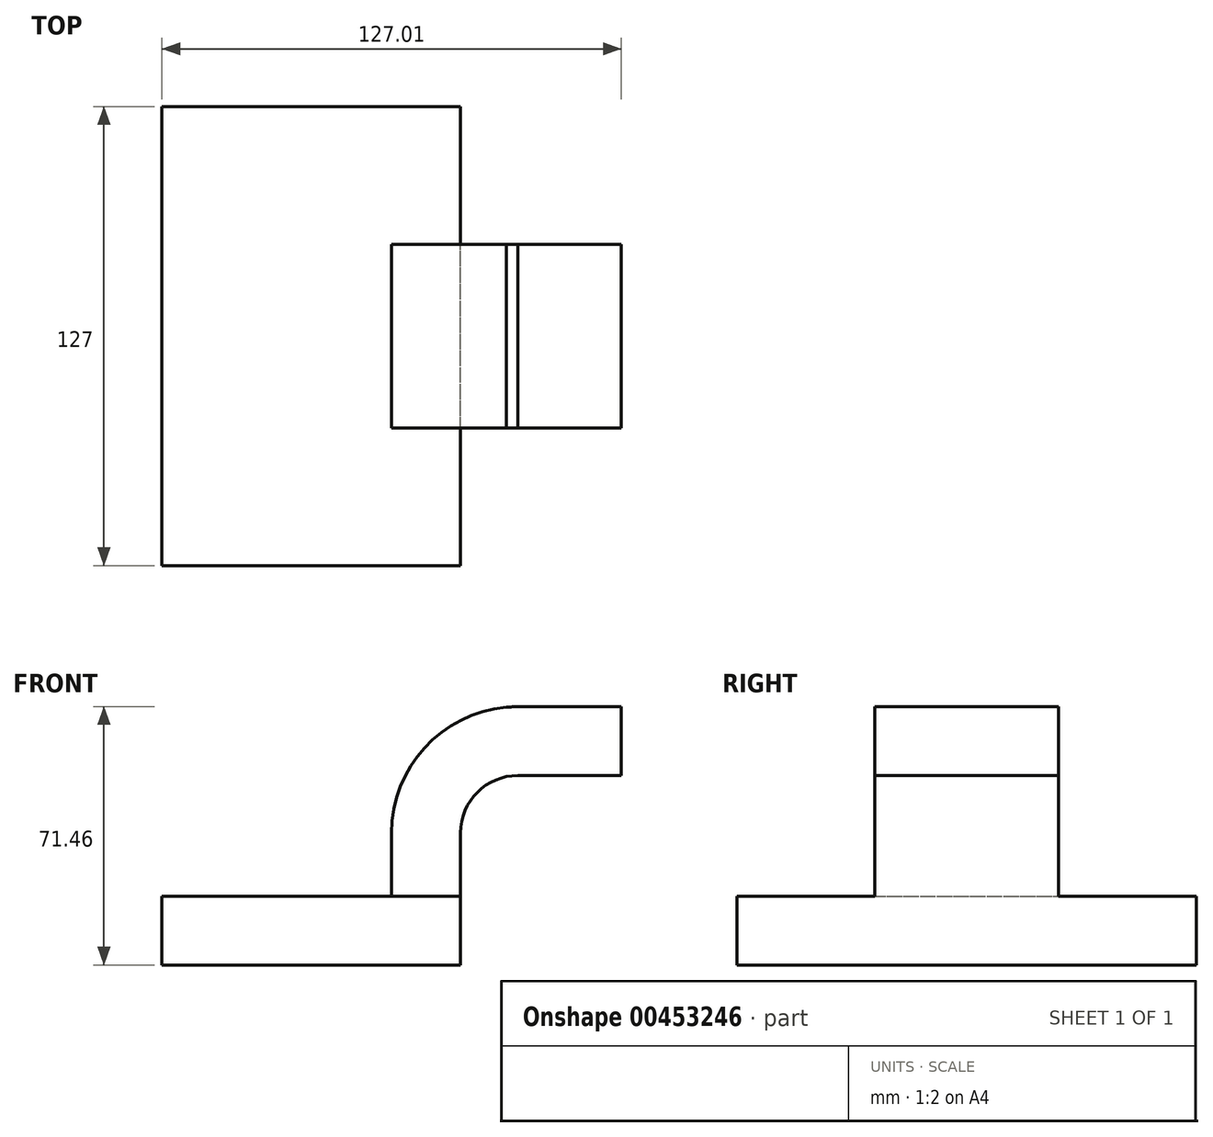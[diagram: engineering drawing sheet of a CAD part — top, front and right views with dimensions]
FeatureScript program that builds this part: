
annotation { "Feature Type Name" : "Feature", "Feature Type Description" : "" }
export const myFeature = defineFeature(function(context is Context, id is Id, definition is map)
    precondition{}
    {
        {
            var Q0;
            Q0=qCreatedBy(makeId("Front.planeOp"),FACE);
            var sketch = newSketch(context, id + "F0", { "sketchPlane" : qUnion([Q0])});
            skLineSegment(sketch, "E0.rect.bottom", {"start": v(-41.28, 9.52) * mm, "end": v(41.28, 9.52) * mm});
            skLineSegment(sketch, "E0.rect.top", {"start": v(-41.28, -9.52) * mm, "end": v(41.28, -9.52) * mm});
            skLineSegment(sketch, "E0.rect.left", {"start": v(-41.28, 9.52) * mm, "end": v(-41.28, -9.52) * mm});
            skLineSegment(sketch, "E0.rect.right", {"start": v(41.28, 9.52) * mm, "end": v(41.28, -9.52) * mm});
            skPoint(sketch, "E0.rect.middle", {"position": v(0, 0) * mm});
            skLineSegment(sketch, "E1", {"start": v(41.28, 9.52) * mm, "end": v(41.28, 27) * mm});
            skArc(sketch, "E2", {"start": v(41.28, 27) * mm, "mid": v(45.92, 38.23) * mm, "end": v(57.15, 42.88) * mm});
            skLineSegment(sketch, "E3", {"start": v(57.15, 42.88) * mm, "end": v(85.72, 42.88) * mm});
            skLineSegment(sketch, "E4.rect.bottom", {"start": v(60.32, 38.1) * mm, "end": v(111.12, 38.1) * mm});
            skLineSegment(sketch, "E4.rect.top", {"start": v(60.32, 66.68) * mm, "end": v(111.12, 66.68) * mm});
            skLineSegment(sketch, "E4.rect.left", {"start": v(60.32, 38.1) * mm, "end": v(60.32, 66.68) * mm});
            skLineSegment(sketch, "E4.rect.right", {"start": v(111.13, 38.1) * mm, "end": v(111.12, 66.68) * mm});
            skPoint(sketch, "E4.rect.middle", {"position": v(85.72, 52.39) * mm});
            skLineSegment(sketch, "E5.0", {"start": v(57.15, 61.93) * mm, "end": v(85.72, 61.93) * mm});
            skArc(sketch, "E5.1", {"start": v(22.23, 27) * mm, "mid": v(32.45, 51.7) * mm, "end": v(57.15, 61.93) * mm});
            skLineSegment(sketch, "E5.2", {"start": v(22.23, 9.52) * mm, "end": v(22.23, 27) * mm});
            skLineSegment(sketch, "E6", {"start": v(85.72, 38.1) * mm, "end": v(85.72, 66.68) * mm});
            skFitSpline(sketch, "E7", {"points": [v(-41.28, 9.53) * mm, v(57.15, 61.93) * mm], "startDerivative": vector(5.2, 92.34) * mm, "endDerivative": vector(120.92, 4.22) * mm});
            skSolve(sketch);
        }
        {
            var Q0;
            Q0=makeQuery(id+"F0.imprint","IMPRINT",FACE,{"disambiguationData":[TD([[makeQuery(id+"F0.imprint","IMPRINT",EDGE,{"derivedFrom":sQuery(id+"F0.wireOp",EDGE,"E0.rect.top")}),1.0]])]});
            extrude(context, id + "F1", {"entities" : qUnion([Q0]), "endBound" : BoundingType.SYMMETRIC, "depth" : 127 * mm});
        }
        {
            var Q0;
            {var subQ9=sQuery(id+"F0.wireOp",EDGE,"E1");Q0=makeQuery(id+"F0.imprint","IMPRINT",FACE,{"disambiguationData":[TD([[makeQuery(id+"F0.imprint","IMPRINT",EDGE,{"derivedFrom":subQ9}),1.0]])]});}
            var Q1;
            {var subQ0=sQuery(id+"F0.wireOp",EDGE,"E6");var subQ1=sQuery(id+"F0.wireOp",EDGE,"E3");var subQ2=makeQuery(id+"F0.imprint","INTERSECT",VERTEX,{"derivedFrom":[subQ1,subQ0]});Q1=makeQuery(id+"F0.imprint","IMPRINT",FACE,{"disambiguationData":[TD([[makeQuery(id+"F0.imprint","IMPRINT",EDGE,{"disambiguationData":[TD([[subQ2,1.0]])],"derivedFrom":subQ1}),1.0]])]});}
            extrude(context, id + "F2", {"entities" : qUnion([Q0, Q1]), "operationType" : NewBodyOperationType.ADD, "endBound" : BoundingType.SYMMETRIC, "depth" : 50.8 * mm});
        }
    });
